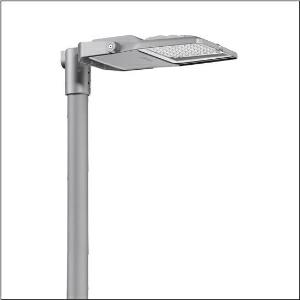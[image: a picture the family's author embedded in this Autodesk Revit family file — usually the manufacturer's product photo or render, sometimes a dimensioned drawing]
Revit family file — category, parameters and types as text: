
# Revit family: floodlight_fl_21_iq_mini___pl64_5xa7772c2e3a_d31a
name_source: partatom
category: Lighting Fixtures
units: mm (PartAtom-declared; Revit-internal decimal feet)

## family parameters
Cut with Voids When Loaded = No
Host = Face
Light Source = No
Part Type = Normal
Room Calculation Point = No
Round Connector Dimension = Use Diameter
Shared = No

## types (1)
- --- (1 x LED, 11790 lm, 87.2 W, 3000K)
    Apparent Load = 87 VA
    CIE Flux Codes = 28 80 98 100 100
    Color Rendering = 70
    Color Temperature = 3000K
    Default Elevation = 1800 mm
    Description = Floodlight FL 21 iQ mini, floodlight, primary light control with lens, of PMMA, primary optical cover: protective disc, of toughened safety glass, transparent, light distribution: PL64, light emission: direct distribution, installation type: surface-mounted, lamps: LED, High Power LED, rated values: 11.790lm | 87,2W | 135,2lm/W (begin service life); end service life: 11.790lm | 92,1W; at 50% lumin. flux: 5.895lm | 40,1W | 147lm/W, colour temperature: 3000K, colour rendering: CRI > 70, light colour: 730, light setting 1 begin service life: 100% | 11.790lm | 87,2W | 135,2lm/W | 3.000K, light setting 1 end service life: 92,1W, further light settings possible, control: Street-Remote, Auto-Match, Temp-Guard, Night-Set, Smart-Wire, Desk-Remote (wireless, voltage-free reading and setting of iQ features in the workshop via application-optimized NFC function/RFID function), optimised constant luminous flux control (CLO 2.0), pre-setting: linear dimming characteristic, with terminal, 6-pole, mains connection: 220..240V, AC, 50/60Hz, luminaire housing, of diecast aluminium, powder-coated, SITECO metallic grey (DB 702S), corrosivity category C5 mid according to DIN EN ISO 12944suitable for swimming poolschlorine-resistant, sealing non-destructively replaceable, please order mast flange separately, mast bracket, of steel, galvanised, powder-coated, protection rating (complete): IP66, insulation class (complete): insulation class II (safety insulation), certification: CE, ENEC, VDE, protection symbol: D, impact resistance: IK08, permissible operating ambient temperature: -40..+40°C, permissible operating ambient temperature for outdoor applications: -40..+50°C, standard: DIN EN 12944, LABS conformity tested according to VDMA 24364:2018-05, packaging unit: 1 piece

Light Distribution: PL64
    Height = 70 mm
    Lamp = 1 x LED
    Lamp Light Flux = 11790 lm
    Lamp Power = 87.2 W
    Lamp count = 1
    Length = 485 mm
    Luminous efficacy = 135 lm/W
    Manufacturer = Siteco
    ModVariant = No
    Model = 5XA7772C2E3A
    Mounting Place = Pole
    Mounting Type = Pole annexe
    Number of Poles = 1
    OnlyDefault = Yes
    Power Factor = 1
    Product Name = Floodlight FL 21 iQ mini | PL64
    Product group = floodlight | pylon annexe
    ProductGroupID = 6201
    Protection Class = Protection class II
    Protection Degree = IP 66
    RLX_Detail_Level = 1
    RLX_Emergency_Light_Flux = 0 lm
    RLX_Emergency_Type = 0
    RLX_Emergency_Type_DB = No
    RlxData = <blob elided: 101589 chars, md5=91288306>
    Socket = socket
    Standby Power = 0 W
    System Light Flux = 11790 lm
    System Power = 87 W
    Type Comments = factory setting: luminous flux: 100 % | dim-lin: 254 | 456 mA
    Type Image = l_1007125.jpg
    URL = http://relux.com
    VarID = @adj_167395
    Voltage = 0 V
    Weight = 0.00 kg
    Width = 337 mm

## geometry (parser evidence)
native form markers: Blend x4, Sweep x13
no freeform markers — native parametric forms only
